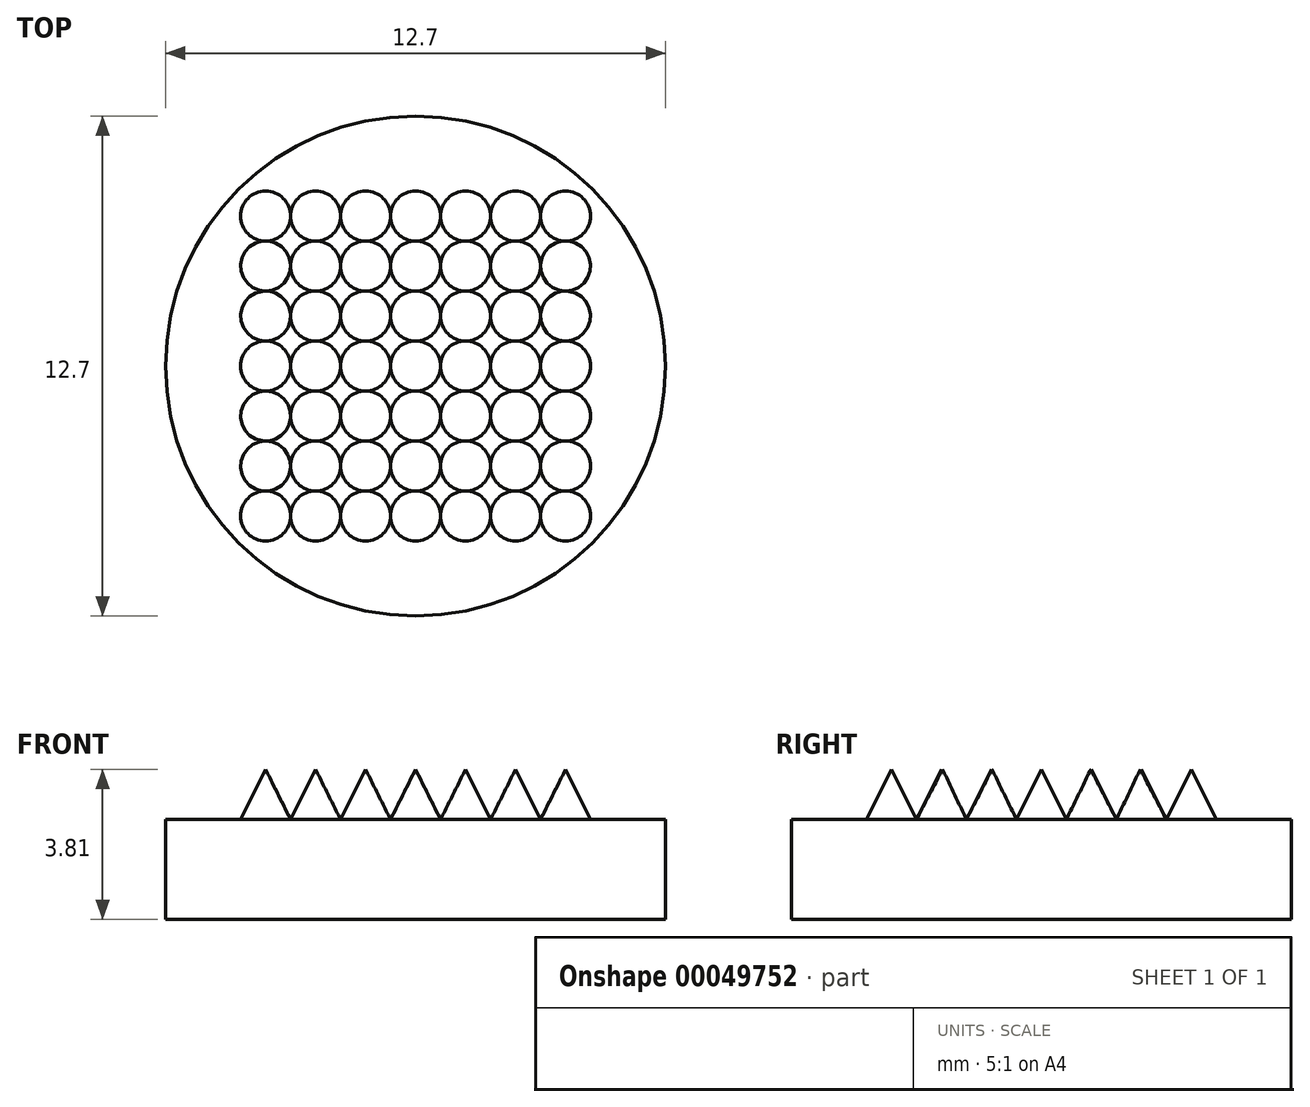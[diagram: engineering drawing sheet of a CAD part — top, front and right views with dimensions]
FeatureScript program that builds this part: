
annotation { "Feature Type Name" : "Feature", "Feature Type Description" : "" }
export const myFeature = defineFeature(function(context is Context, id is Id, definition is map)
    precondition{}
    {
        {
            var Q0;
            Q0=qCreatedBy(makeId("Top.planeOp"),FACE);
            var sketch = newSketch(context, id + "F0", { "sketchPlane" : qUnion([Q0])});
            skCircle(sketch, "E0", {"center": v(0, 0) * mm, "radius": 6.35 * mm});
            skSolve(sketch);
        }
        {
            var Q0;
            Q0=qCreatedBy(makeId("Top.planeOp"),FACE);
            var sketch = newSketch(context, id + "F1", { "sketchPlane" : qUnion([Q0])});
            skCircle(sketch, "E1", {"center": v(0, 0) * mm, "radius": 0.64 * mm});
            skCircle(sketch, "E2", {"center": v(1.27, 0) * mm, "radius": 0.64 * mm});
            skCircle(sketch, "E3", {"center": v(2.54, 0) * mm, "radius": 0.64 * mm});
            skCircle(sketch, "E4", {"center": v(1.27, -1.27) * mm, "radius": 0.64 * mm});
            skCircle(sketch, "E5", {"center": v(2.54, -1.27) * mm, "radius": 0.64 * mm});
            skCircle(sketch, "E6", {"center": v(1.27, -2.54) * mm, "radius": 0.64 * mm});
            skCircle(sketch, "E7", {"center": v(1.27, -3.81) * mm, "radius": 0.64 * mm});
            skCircle(sketch, "E8", {"center": v(2.54, -2.54) * mm, "radius": 0.64 * mm});
            skCircle(sketch, "E9", {"center": v(2.54, -3.81) * mm, "radius": 0.64 * mm});
            skCircle(sketch, "E10", {"center": v(0, -1.27) * mm, "radius": 0.64 * mm});
            skCircle(sketch, "E11", {"center": v(0, -2.54) * mm, "radius": 0.64 * mm});
            skCircle(sketch, "E12", {"center": v(0, -3.81) * mm, "radius": 0.64 * mm});
            skCircle(sketch, "E13", {"center": v(3.81, 0) * mm, "radius": 0.64 * mm});
            skCircle(sketch, "E14", {"center": v(3.81, -1.27) * mm, "radius": 0.64 * mm});
            skCircle(sketch, "E15", {"center": v(3.81, -2.54) * mm, "radius": 0.64 * mm});
            skCircle(sketch, "E16", {"center": v(3.81, -3.81) * mm, "radius": 0.64 * mm});
            skSolve(sketch);
        }
        {
            var Q0;
            Q0=makeQuery(id+"F1.imprint","IMPRINT",FACE,{"disambiguationData":[TD([[makeQuery(id+"F1.imprint","IMPRINT",EDGE,{"derivedFrom":sQuery(id+"F1.wireOp",EDGE,"E1")}),1.0]])]});
            cPlane(context, id + "F2", {"entities" : qUnion([Q0]), "cplaneType" : CPlaneType.OFFSET, "offset" : 1.27 * mm, "width" : 152.4 * mm, "height" : 152.4 * mm});
        }
        {
            var Q0;
            Q0=qCreatedBy(id+"F2.planeOp",FACE);
            var sketch = newSketch(context, id + "F3", { "sketchPlane" : qUnion([Q0])});
            skPoint(sketch, "E17", {"position": v(0, 0) * mm});
            skPoint(sketch, "E18", {"position": v(0, -1.27) * mm});
            skPoint(sketch, "E19", {"position": v(0, -2.54) * mm});
            skPoint(sketch, "E20", {"position": v(1.27, 0) * mm});
            skPoint(sketch, "E21", {"position": v(1.27, -1.27) * mm});
            skPoint(sketch, "E22", {"position": v(1.27, -2.54) * mm});
            skPoint(sketch, "E23", {"position": v(1.27, -3.81) * mm});
            skPoint(sketch, "E24", {"position": v(2.54, 0) * mm});
            skPoint(sketch, "E25", {"position": v(2.54, -1.27) * mm});
            skPoint(sketch, "E26", {"position": v(2.54, -2.54) * mm});
            skPoint(sketch, "E27", {"position": v(2.54, -3.81) * mm});
            skPoint(sketch, "E28", {"position": v(0, -3.81) * mm});
            skPoint(sketch, "E29", {"position": v(3.81, 0) * mm});
            skPoint(sketch, "E30", {"position": v(3.8, -1.25) * mm});
            skPoint(sketch, "E31", {"position": v(3.81, -2.51) * mm});
            skPoint(sketch, "E32", {"position": v(3.81, -3.81) * mm});
            skSolve(sketch);
        }
        {
            var Q0;
            {var subQ0=sQuery(id+"F1.wireOp",EDGE,"E1");var subQ1=makeQuery(id+"F1.imprint","INTERSECT",VERTEX,{"derivedFrom":[subQ0,sQuery(id+"F1.wireOp",EDGE,"E2")]});Q0=makeQuery(id+"F1.imprint","IMPRINT",FACE,{"disambiguationData":[TD([[makeQuery(id+"F1.imprint","IMPRINT",EDGE,{"disambiguationData":[TD([[subQ1,-1.0]])],"derivedFrom":subQ0}),1.0]])]});}
            var Q1;
            Q1=sQuery(id+"F3.wireOp",VERTEX,"E17");
            loft(context, id + "F4", {"sheetProfilesArray" : [{ "sheetProfileEntities" : qUnion([Q0]) }, { "sheetProfileEntities" : qUnion([Q1]) }]});
        }
        {
            var Q0;
            Q0=makeQuery(id+"F0.imprint","IMPRINT",FACE,{"disambiguationData":[TD([[makeQuery(id+"F0.imprint","IMPRINT",EDGE,{"derivedFrom":sQuery(id+"F0.wireOp",EDGE,"E0")}),1.0]])]});
            extrude(context, id + "F5", {"entities" : qUnion([Q0]), "oppositeDirection" : true, "depth" : 2.54 * mm});
        }
        {
            var Q1;
            {var subQ0=sQuery(id+"F1.wireOp",EDGE,"E10");var subQ1=makeQuery(id+"F1.imprint","INTERSECT",VERTEX,{"derivedFrom":[sQuery(id+"F1.wireOp",EDGE,"E1"),subQ0]});Q1=makeQuery(id+"F1.imprint","IMPRINT",FACE,{"disambiguationData":[TD([[makeQuery(id+"F1.imprint","IMPRINT",EDGE,{"disambiguationData":[TD([[subQ1,1.0]])],"derivedFrom":subQ0}),1.0]])]});}
            var Q2;
            Q2=sQuery(id+"F3.wireOp",VERTEX,"E18");
            loft(context, id + "F6", {"sheetProfilesArray" : [{ "sheetProfileEntities" : qUnion([Q1]) }, { "sheetProfileEntities" : qUnion([Q2]) }]});
        }
        {
            var Q1;
            {var subQ0=sQuery(id+"F1.wireOp",EDGE,"E11");var subQ1=makeQuery(id+"F1.imprint","INTERSECT",VERTEX,{"derivedFrom":[sQuery(id+"F1.wireOp",EDGE,"E10"),subQ0]});Q1=makeQuery(id+"F1.imprint","IMPRINT",FACE,{"disambiguationData":[TD([[makeQuery(id+"F1.imprint","IMPRINT",EDGE,{"disambiguationData":[TD([[subQ1,1.0]])],"derivedFrom":subQ0}),1.0]])]});}
            var Q2;
            Q2=sQuery(id+"F3.wireOp",VERTEX,"E19");
            loft(context, id + "F7", {"sheetProfilesArray" : [{ "sheetProfileEntities" : qUnion([Q1]) }, { "sheetProfileEntities" : qUnion([Q2]) }]});
        }
        {
            var Q1;
            {var subQ0=sQuery(id+"F1.wireOp",EDGE,"E12");var subQ1=makeQuery(id+"F1.imprint","INTERSECT",VERTEX,{"derivedFrom":[sQuery(id+"F1.wireOp",EDGE,"E7"),subQ0]});Q1=makeQuery(id+"F1.imprint","IMPRINT",FACE,{"disambiguationData":[TD([[makeQuery(id+"F1.imprint","IMPRINT",EDGE,{"disambiguationData":[TD([[subQ1,-1.0]])],"derivedFrom":subQ0}),1.0]])]});}
            var Q2;
            Q2=sQuery(id+"F3.wireOp",VERTEX,"E28");
            loft(context, id + "F8", {"sheetProfilesArray" : [{ "sheetProfileEntities" : qUnion([Q1]) }, { "sheetProfileEntities" : qUnion([Q2]) }]});
        }
        {
            var Q1;
            {var subQ0=sQuery(id+"F1.wireOp",EDGE,"E2");var subQ1=makeQuery(id+"F1.imprint","INTERSECT",VERTEX,{"derivedFrom":[sQuery(id+"F1.wireOp",EDGE,"E1"),subQ0]});Q1=makeQuery(id+"F1.imprint","IMPRINT",FACE,{"disambiguationData":[TD([[makeQuery(id+"F1.imprint","IMPRINT",EDGE,{"disambiguationData":[TD([[subQ1,1.0]])],"derivedFrom":subQ0}),1.0]])]});}
            var Q2;
            Q2=sQuery(id+"F3.wireOp",VERTEX,"E20");
            loft(context, id + "F9", {"sheetProfilesArray" : [{ "sheetProfileEntities" : qUnion([Q1]) }, { "sheetProfileEntities" : qUnion([Q2]) }]});
        }
        {
            var Q1;
            {var subQ0=sQuery(id+"F1.wireOp",EDGE,"E4");var subQ1=makeQuery(id+"F1.imprint","INTERSECT",VERTEX,{"derivedFrom":[sQuery(id+"F1.wireOp",EDGE,"E2"),subQ0]});Q1=makeQuery(id+"F1.imprint","IMPRINT",FACE,{"disambiguationData":[TD([[makeQuery(id+"F1.imprint","IMPRINT",EDGE,{"disambiguationData":[TD([[subQ1,1.0]])],"derivedFrom":subQ0}),1.0]])]});}
            var Q2;
            Q2=sQuery(id+"F3.wireOp",VERTEX,"E21");
            loft(context, id + "F10", {"sheetProfilesArray" : [{ "sheetProfileEntities" : qUnion([Q1]) }, { "sheetProfileEntities" : qUnion([Q2]) }]});
        }
        {
            var Q1;
            {var subQ0=sQuery(id+"F1.wireOp",EDGE,"E6");var subQ1=makeQuery(id+"F1.imprint","INTERSECT",VERTEX,{"derivedFrom":[sQuery(id+"F1.wireOp",EDGE,"E4"),subQ0]});Q1=makeQuery(id+"F1.imprint","IMPRINT",FACE,{"disambiguationData":[TD([[makeQuery(id+"F1.imprint","IMPRINT",EDGE,{"disambiguationData":[TD([[subQ1,1.0]])],"derivedFrom":subQ0}),1.0]])]});}
            var Q2;
            Q2=sQuery(id+"F3.wireOp",VERTEX,"E22");
            loft(context, id + "F11", {"sheetProfilesArray" : [{ "sheetProfileEntities" : qUnion([Q1]) }, { "sheetProfileEntities" : qUnion([Q2]) }]});
        }
        {
            var Q1;
            {var subQ0=sQuery(id+"F1.wireOp",EDGE,"E7");var subQ1=makeQuery(id+"F1.imprint","INTERSECT",VERTEX,{"derivedFrom":[subQ0,sQuery(id+"F1.wireOp",EDGE,"E9")]});Q1=makeQuery(id+"F1.imprint","IMPRINT",FACE,{"disambiguationData":[TD([[makeQuery(id+"F1.imprint","IMPRINT",EDGE,{"disambiguationData":[TD([[subQ1,-1.0]])],"derivedFrom":subQ0}),1.0]])]});}
            var Q2;
            Q2=sQuery(id+"F3.wireOp",VERTEX,"E23");
            loft(context, id + "F12", {"sheetProfilesArray" : [{ "sheetProfileEntities" : qUnion([Q1]) }, { "sheetProfileEntities" : qUnion([Q2]) }]});
        }
        {
            var Q1;
            {var subQ0=sQuery(id+"F1.wireOp",EDGE,"E3");var subQ1=makeQuery(id+"F1.imprint","INTERSECT",VERTEX,{"derivedFrom":[sQuery(id+"F1.wireOp",EDGE,"E2"),subQ0]});Q1=makeQuery(id+"F1.imprint","IMPRINT",FACE,{"disambiguationData":[TD([[makeQuery(id+"F1.imprint","IMPRINT",EDGE,{"disambiguationData":[TD([[subQ1,-1.0]])],"derivedFrom":subQ0}),1.0]])]});}
            var Q2;
            Q2=sQuery(id+"F3.wireOp",VERTEX,"E24");
            loft(context, id + "F13", {"sheetProfilesArray" : [{ "sheetProfileEntities" : qUnion([Q1]) }, { "sheetProfileEntities" : qUnion([Q2]) }]});
        }
        {
            var Q1;
            {var subQ0=sQuery(id+"F1.wireOp",EDGE,"E5");var subQ1=makeQuery(id+"F1.imprint","INTERSECT",VERTEX,{"derivedFrom":[sQuery(id+"F1.wireOp",EDGE,"E3"),subQ0]});Q1=makeQuery(id+"F1.imprint","IMPRINT",FACE,{"disambiguationData":[TD([[makeQuery(id+"F1.imprint","IMPRINT",EDGE,{"disambiguationData":[TD([[subQ1,-1.0]])],"derivedFrom":subQ0}),1.0]])]});}
            var Q2;
            Q2=sQuery(id+"F3.wireOp",VERTEX,"E25");
            loft(context, id + "F14", {"sheetProfilesArray" : [{ "sheetProfileEntities" : qUnion([Q1]) }, { "sheetProfileEntities" : qUnion([Q2]) }]});
        }
        {
            var Q1;
            {var subQ0=sQuery(id+"F1.wireOp",EDGE,"E8");var subQ1=makeQuery(id+"F1.imprint","INTERSECT",VERTEX,{"derivedFrom":[sQuery(id+"F1.wireOp",EDGE,"E5"),subQ0]});Q1=makeQuery(id+"F1.imprint","IMPRINT",FACE,{"disambiguationData":[TD([[makeQuery(id+"F1.imprint","IMPRINT",EDGE,{"disambiguationData":[TD([[subQ1,-1.0]])],"derivedFrom":subQ0}),1.0]])]});}
            var Q2;
            Q2=sQuery(id+"F3.wireOp",VERTEX,"E26");
            loft(context, id + "F15", {"sheetProfilesArray" : [{ "sheetProfileEntities" : qUnion([Q1]) }, { "sheetProfileEntities" : qUnion([Q2]) }]});
        }
        {
            var Q1;
            {var subQ0=sQuery(id+"F1.wireOp",EDGE,"E9");var subQ1=makeQuery(id+"F1.imprint","INTERSECT",VERTEX,{"derivedFrom":[sQuery(id+"F1.wireOp",EDGE,"E7"),subQ0]});Q1=makeQuery(id+"F1.imprint","IMPRINT",FACE,{"disambiguationData":[TD([[makeQuery(id+"F1.imprint","IMPRINT",EDGE,{"disambiguationData":[TD([[subQ1,1.0]])],"derivedFrom":subQ0}),1.0]])]});}
            var Q2;
            Q2=sQuery(id+"F3.wireOp",VERTEX,"E27");
            loft(context, id + "F16", {"sheetProfilesArray" : [{ "sheetProfileEntities" : qUnion([Q1]) }, { "sheetProfileEntities" : qUnion([Q2]) }]});
        }
        {
            var Q1;
            {var subQ0=sQuery(id+"F1.wireOp",EDGE,"E13");var subQ1=makeQuery(id+"F1.imprint","INTERSECT",VERTEX,{"derivedFrom":[sQuery(id+"F1.wireOp",EDGE,"E3"),subQ0]});Q1=makeQuery(id+"F1.imprint","IMPRINT",FACE,{"disambiguationData":[TD([[makeQuery(id+"F1.imprint","IMPRINT",EDGE,{"disambiguationData":[TD([[subQ1,-1.0]])],"derivedFrom":subQ0}),1.0]])]});}
            var Q2;
            Q2=sQuery(id+"F3.wireOp",VERTEX,"E29");
            loft(context, id + "F17", {"sheetProfilesArray" : [{ "sheetProfileEntities" : qUnion([Q1]) }, { "sheetProfileEntities" : qUnion([Q2]) }]});
        }
        {
            var Q1;
            {var subQ0=sQuery(id+"F1.wireOp",EDGE,"E14");var subQ1=makeQuery(id+"F1.imprint","INTERSECT",VERTEX,{"derivedFrom":[sQuery(id+"F1.wireOp",EDGE,"E13"),subQ0]});Q1=makeQuery(id+"F1.imprint","IMPRINT",FACE,{"disambiguationData":[TD([[makeQuery(id+"F1.imprint","IMPRINT",EDGE,{"disambiguationData":[TD([[subQ1,-1.0]])],"derivedFrom":subQ0}),1.0]])]});}
            var Q2;
            Q2=sQuery(id+"F3.wireOp",VERTEX,"E30");
            loft(context, id + "F18", {"sheetProfilesArray" : [{ "sheetProfileEntities" : qUnion([Q1]) }, { "sheetProfileEntities" : qUnion([Q2]) }]});
        }
        {
            var Q1;
            {var subQ0=sQuery(id+"F1.wireOp",EDGE,"E15");var subQ1=makeQuery(id+"F1.imprint","INTERSECT",VERTEX,{"derivedFrom":[sQuery(id+"F1.wireOp",EDGE,"E14"),subQ0]});Q1=makeQuery(id+"F1.imprint","IMPRINT",FACE,{"disambiguationData":[TD([[makeQuery(id+"F1.imprint","IMPRINT",EDGE,{"disambiguationData":[TD([[subQ1,-1.0]])],"derivedFrom":subQ0}),1.0]])]});}
            var Q2;
            Q2=sQuery(id+"F3.wireOp",VERTEX,"E31");
            loft(context, id + "F19", {"sheetProfilesArray" : [{ "sheetProfileEntities" : qUnion([Q1]) }, { "sheetProfileEntities" : qUnion([Q2]) }]});
        }
        {
            var Q1;
            {var subQ0=sQuery(id+"F1.wireOp",EDGE,"E16");var subQ1=makeQuery(id+"F1.imprint","INTERSECT",VERTEX,{"derivedFrom":[sQuery(id+"F1.wireOp",EDGE,"E9"),subQ0]});Q1=makeQuery(id+"F1.imprint","IMPRINT",FACE,{"disambiguationData":[TD([[makeQuery(id+"F1.imprint","IMPRINT",EDGE,{"disambiguationData":[TD([[subQ1,1.0]])],"derivedFrom":subQ0}),1.0]])]});}
            var Q2;
            Q2=sQuery(id+"F3.wireOp",VERTEX,"E32");
            loft(context, id + "F20", {"sheetProfilesArray" : [{ "sheetProfileEntities" : qUnion([Q1]) }, { "sheetProfileEntities" : qUnion([Q2]) }]});
        }
        {
            var Q0;
            {var subQ0=sQuery(id+"F1.wireOp",EDGE,"E1");var subQ1=makeQuery(id+"F1.imprint","INTERSECT",VERTEX,{"derivedFrom":[subQ0,sQuery(id+"F1.wireOp",EDGE,"E2")]});Q0=makeQuery(id+"F4.opLoft","SWEPT_BODY",BODY,{"disambiguationData":[OSD([makeQuery(id+"F1.imprint","IMPRINT",FACE,{"disambiguationData":[TD([[makeQuery(id+"F1.imprint","IMPRINT",EDGE,{"disambiguationData":[TD([[subQ1,-1.0]])],"derivedFrom":subQ0}),1.0]])]}),sQuery(id+"F3.wireOp",VERTEX,"E17")])]});}
            var Q1;
            {var subQ0=sQuery(id+"F1.wireOp",EDGE,"E10");var subQ1=makeQuery(id+"F1.imprint","INTERSECT",VERTEX,{"derivedFrom":[sQuery(id+"F1.wireOp",EDGE,"E1"),subQ0]});Q1=makeQuery(id+"F6.opLoft","SWEPT_BODY",BODY,{"disambiguationData":[OSD([makeQuery(id+"F1.imprint","IMPRINT",FACE,{"disambiguationData":[TD([[makeQuery(id+"F1.imprint","IMPRINT",EDGE,{"disambiguationData":[TD([[subQ1,1.0]])],"derivedFrom":subQ0}),1.0]])]}),sQuery(id+"F3.wireOp",VERTEX,"E18")])]});}
            var Q2;
            {var subQ0=sQuery(id+"F1.wireOp",EDGE,"E11");var subQ1=makeQuery(id+"F1.imprint","INTERSECT",VERTEX,{"derivedFrom":[sQuery(id+"F1.wireOp",EDGE,"E10"),subQ0]});Q2=makeQuery(id+"F7.opLoft","SWEPT_BODY",BODY,{"disambiguationData":[OSD([makeQuery(id+"F1.imprint","IMPRINT",FACE,{"disambiguationData":[TD([[makeQuery(id+"F1.imprint","IMPRINT",EDGE,{"disambiguationData":[TD([[subQ1,1.0]])],"derivedFrom":subQ0}),1.0]])]}),sQuery(id+"F3.wireOp",VERTEX,"E19")])]});}
            var Q3;
            {var subQ0=sQuery(id+"F1.wireOp",EDGE,"E12");var subQ1=makeQuery(id+"F1.imprint","INTERSECT",VERTEX,{"derivedFrom":[sQuery(id+"F1.wireOp",EDGE,"E7"),subQ0]});Q3=makeQuery(id+"F8.opLoft","SWEPT_BODY",BODY,{"disambiguationData":[OSD([makeQuery(id+"F1.imprint","IMPRINT",FACE,{"disambiguationData":[TD([[makeQuery(id+"F1.imprint","IMPRINT",EDGE,{"disambiguationData":[TD([[subQ1,-1.0]])],"derivedFrom":subQ0}),1.0]])]}),sQuery(id+"F3.wireOp",VERTEX,"E28")])]});}
            var Q4;
            {var subQ0=sQuery(id+"F1.wireOp",EDGE,"E7");var subQ1=makeQuery(id+"F1.imprint","INTERSECT",VERTEX,{"derivedFrom":[subQ0,sQuery(id+"F1.wireOp",EDGE,"E9")]});Q4=makeQuery(id+"F12.opLoft","SWEPT_BODY",BODY,{"disambiguationData":[OSD([makeQuery(id+"F1.imprint","IMPRINT",FACE,{"disambiguationData":[TD([[makeQuery(id+"F1.imprint","IMPRINT",EDGE,{"disambiguationData":[TD([[subQ1,-1.0]])],"derivedFrom":subQ0}),1.0]])]}),sQuery(id+"F3.wireOp",VERTEX,"E23")])]});}
            var Q5;
            {var subQ0=sQuery(id+"F1.wireOp",EDGE,"E6");var subQ1=makeQuery(id+"F1.imprint","INTERSECT",VERTEX,{"derivedFrom":[sQuery(id+"F1.wireOp",EDGE,"E4"),subQ0]});Q5=makeQuery(id+"F11.opLoft","SWEPT_BODY",BODY,{"disambiguationData":[OSD([makeQuery(id+"F1.imprint","IMPRINT",FACE,{"disambiguationData":[TD([[makeQuery(id+"F1.imprint","IMPRINT",EDGE,{"disambiguationData":[TD([[subQ1,1.0]])],"derivedFrom":subQ0}),1.0]])]}),sQuery(id+"F3.wireOp",VERTEX,"E22")])]});}
            var Q6;
            {var subQ0=sQuery(id+"F1.wireOp",EDGE,"E4");var subQ1=makeQuery(id+"F1.imprint","INTERSECT",VERTEX,{"derivedFrom":[sQuery(id+"F1.wireOp",EDGE,"E2"),subQ0]});Q6=makeQuery(id+"F10.opLoft","SWEPT_BODY",BODY,{"disambiguationData":[OSD([makeQuery(id+"F1.imprint","IMPRINT",FACE,{"disambiguationData":[TD([[makeQuery(id+"F1.imprint","IMPRINT",EDGE,{"disambiguationData":[TD([[subQ1,1.0]])],"derivedFrom":subQ0}),1.0]])]}),sQuery(id+"F3.wireOp",VERTEX,"E21")])]});}
            var Q7;
            {var subQ0=sQuery(id+"F1.wireOp",EDGE,"E2");var subQ1=makeQuery(id+"F1.imprint","INTERSECT",VERTEX,{"derivedFrom":[sQuery(id+"F1.wireOp",EDGE,"E1"),subQ0]});Q7=makeQuery(id+"F9.opLoft","SWEPT_BODY",BODY,{"disambiguationData":[OSD([makeQuery(id+"F1.imprint","IMPRINT",FACE,{"disambiguationData":[TD([[makeQuery(id+"F1.imprint","IMPRINT",EDGE,{"disambiguationData":[TD([[subQ1,1.0]])],"derivedFrom":subQ0}),1.0]])]}),sQuery(id+"F3.wireOp",VERTEX,"E20")])]});}
            var Q8;
            {var subQ0=sQuery(id+"F1.wireOp",EDGE,"E13");var subQ1=makeQuery(id+"F1.imprint","INTERSECT",VERTEX,{"derivedFrom":[sQuery(id+"F1.wireOp",EDGE,"E3"),subQ0]});Q8=makeQuery(id+"F17.opLoft","SWEPT_BODY",BODY,{"disambiguationData":[OSD([makeQuery(id+"F1.imprint","IMPRINT",FACE,{"disambiguationData":[TD([[makeQuery(id+"F1.imprint","IMPRINT",EDGE,{"disambiguationData":[TD([[subQ1,-1.0]])],"derivedFrom":subQ0}),1.0]])]}),sQuery(id+"F3.wireOp",VERTEX,"E29")])]});}
            var Q9;
            {var subQ0=sQuery(id+"F1.wireOp",EDGE,"E3");var subQ1=makeQuery(id+"F1.imprint","INTERSECT",VERTEX,{"derivedFrom":[sQuery(id+"F1.wireOp",EDGE,"E2"),subQ0]});Q9=makeQuery(id+"F13.opLoft","SWEPT_BODY",BODY,{"disambiguationData":[OSD([makeQuery(id+"F1.imprint","IMPRINT",FACE,{"disambiguationData":[TD([[makeQuery(id+"F1.imprint","IMPRINT",EDGE,{"disambiguationData":[TD([[subQ1,1.0]])],"derivedFrom":subQ0}),1.0]])]}),sQuery(id+"F3.wireOp",VERTEX,"E24")])]});}
            var Q10;
            {var subQ0=sQuery(id+"F1.wireOp",EDGE,"E5");var subQ1=makeQuery(id+"F1.imprint","INTERSECT",VERTEX,{"derivedFrom":[sQuery(id+"F1.wireOp",EDGE,"E3"),subQ0]});Q10=makeQuery(id+"F14.opLoft","SWEPT_BODY",BODY,{"disambiguationData":[OSD([makeQuery(id+"F1.imprint","IMPRINT",FACE,{"disambiguationData":[TD([[makeQuery(id+"F1.imprint","IMPRINT",EDGE,{"disambiguationData":[TD([[subQ1,1.0]])],"derivedFrom":subQ0}),1.0]])]}),sQuery(id+"F3.wireOp",VERTEX,"E25")])]});}
            var Q11;
            {var subQ0=sQuery(id+"F1.wireOp",EDGE,"E14");var subQ1=makeQuery(id+"F1.imprint","INTERSECT",VERTEX,{"derivedFrom":[sQuery(id+"F1.wireOp",EDGE,"E13"),subQ0]});Q11=makeQuery(id+"F18.opLoft","SWEPT_BODY",BODY,{"disambiguationData":[OSD([makeQuery(id+"F1.imprint","IMPRINT",FACE,{"disambiguationData":[TD([[makeQuery(id+"F1.imprint","IMPRINT",EDGE,{"disambiguationData":[TD([[subQ1,-1.0]])],"derivedFrom":subQ0}),1.0]])]}),sQuery(id+"F3.wireOp",VERTEX,"E30")])]});}
            var Q12;
            {var subQ0=sQuery(id+"F1.wireOp",EDGE,"E15");var subQ1=makeQuery(id+"F1.imprint","INTERSECT",VERTEX,{"derivedFrom":[sQuery(id+"F1.wireOp",EDGE,"E14"),subQ0]});Q12=makeQuery(id+"F19.opLoft","SWEPT_BODY",BODY,{"disambiguationData":[OSD([makeQuery(id+"F1.imprint","IMPRINT",FACE,{"disambiguationData":[TD([[makeQuery(id+"F1.imprint","IMPRINT",EDGE,{"disambiguationData":[TD([[subQ1,-1.0]])],"derivedFrom":subQ0}),1.0]])]}),sQuery(id+"F3.wireOp",VERTEX,"E31")])]});}
            var Q13;
            {var subQ0=sQuery(id+"F1.wireOp",EDGE,"E8");var subQ1=makeQuery(id+"F1.imprint","INTERSECT",VERTEX,{"derivedFrom":[sQuery(id+"F1.wireOp",EDGE,"E5"),subQ0]});Q13=makeQuery(id+"F15.opLoft","SWEPT_BODY",BODY,{"disambiguationData":[OSD([makeQuery(id+"F1.imprint","IMPRINT",FACE,{"disambiguationData":[TD([[makeQuery(id+"F1.imprint","IMPRINT",EDGE,{"disambiguationData":[TD([[subQ1,1.0]])],"derivedFrom":subQ0}),1.0]])]}),sQuery(id+"F3.wireOp",VERTEX,"E26")])]});}
            var Q14;
            {var subQ0=sQuery(id+"F1.wireOp",EDGE,"E9");var subQ1=makeQuery(id+"F1.imprint","INTERSECT",VERTEX,{"derivedFrom":[subQ0,sQuery(id+"F1.wireOp",EDGE,"E16")]});Q14=makeQuery(id+"F16.opLoft","SWEPT_BODY",BODY,{"disambiguationData":[OSD([makeQuery(id+"F1.imprint","IMPRINT",FACE,{"disambiguationData":[TD([[makeQuery(id+"F1.imprint","IMPRINT",EDGE,{"disambiguationData":[TD([[subQ1,-1.0]])],"derivedFrom":subQ0}),1.0]])]}),sQuery(id+"F3.wireOp",VERTEX,"E27")])]});}
            var Q15;
            {var subQ0=sQuery(id+"F1.wireOp",EDGE,"E16");var subQ1=makeQuery(id+"F1.imprint","INTERSECT",VERTEX,{"derivedFrom":[sQuery(id+"F1.wireOp",EDGE,"E9"),subQ0]});Q15=makeQuery(id+"F20.opLoft","SWEPT_BODY",BODY,{"disambiguationData":[OSD([makeQuery(id+"F1.imprint","IMPRINT",FACE,{"disambiguationData":[TD([[makeQuery(id+"F1.imprint","IMPRINT",EDGE,{"disambiguationData":[TD([[subQ1,1.0]])],"derivedFrom":subQ0}),1.0]])]}),sQuery(id+"F3.wireOp",VERTEX,"E32")])]});}
            var Q16;
            Q16=qCreatedBy(makeId("Right.planeOp"),FACE);
            mirror(context, id + "F21", {"entities" : qUnion([Q0, Q1, Q2, Q3, Q4, Q5, Q6, Q7, Q8, Q9, Q10, Q11, Q12, Q13, Q14, Q15]), "mirrorPlane" : qUnion([Q16])});
        }
        {
            var Q0;
            {var subQ0=sQuery(id+"F1.wireOp",EDGE,"E13");var subQ1=makeQuery(id+"F1.imprint","INTERSECT",VERTEX,{"derivedFrom":[sQuery(id+"F1.wireOp",EDGE,"E3"),subQ0]});Q0=makeQuery(id+"F21.opPattern","COPY",BODY,{"derivedFrom":makeQuery(id+"F17.opLoft","SWEPT_BODY",BODY,{"disambiguationData":[OSD([makeQuery(id+"F1.imprint","IMPRINT",FACE,{"disambiguationData":[TD([[makeQuery(id+"F1.imprint","IMPRINT",EDGE,{"disambiguationData":[TD([[subQ1,-1.0]])],"derivedFrom":subQ0}),1.0]])]}),sQuery(id+"F3.wireOp",VERTEX,"E29")])]}),"instanceName":"1"});}
            var Q1;
            {var subQ0=sQuery(id+"F1.wireOp",EDGE,"E14");var subQ1=makeQuery(id+"F1.imprint","INTERSECT",VERTEX,{"derivedFrom":[sQuery(id+"F1.wireOp",EDGE,"E13"),subQ0]});Q1=makeQuery(id+"F21.opPattern","COPY",BODY,{"derivedFrom":makeQuery(id+"F18.opLoft","SWEPT_BODY",BODY,{"disambiguationData":[OSD([makeQuery(id+"F1.imprint","IMPRINT",FACE,{"disambiguationData":[TD([[makeQuery(id+"F1.imprint","IMPRINT",EDGE,{"disambiguationData":[TD([[subQ1,-1.0]])],"derivedFrom":subQ0}),1.0]])]}),sQuery(id+"F3.wireOp",VERTEX,"E30")])]}),"instanceName":"1"});}
            var Q2;
            {var subQ0=sQuery(id+"F1.wireOp",EDGE,"E15");var subQ1=makeQuery(id+"F1.imprint","INTERSECT",VERTEX,{"derivedFrom":[sQuery(id+"F1.wireOp",EDGE,"E14"),subQ0]});Q2=makeQuery(id+"F21.opPattern","COPY",BODY,{"derivedFrom":makeQuery(id+"F19.opLoft","SWEPT_BODY",BODY,{"disambiguationData":[OSD([makeQuery(id+"F1.imprint","IMPRINT",FACE,{"disambiguationData":[TD([[makeQuery(id+"F1.imprint","IMPRINT",EDGE,{"disambiguationData":[TD([[subQ1,-1.0]])],"derivedFrom":subQ0}),1.0]])]}),sQuery(id+"F3.wireOp",VERTEX,"E31")])]}),"instanceName":"1"});}
            var Q3;
            {var subQ0=sQuery(id+"F1.wireOp",EDGE,"E16");var subQ1=makeQuery(id+"F1.imprint","INTERSECT",VERTEX,{"derivedFrom":[sQuery(id+"F1.wireOp",EDGE,"E9"),subQ0]});Q3=makeQuery(id+"F21.opPattern","COPY",BODY,{"derivedFrom":makeQuery(id+"F20.opLoft","SWEPT_BODY",BODY,{"disambiguationData":[OSD([makeQuery(id+"F1.imprint","IMPRINT",FACE,{"disambiguationData":[TD([[makeQuery(id+"F1.imprint","IMPRINT",EDGE,{"disambiguationData":[TD([[subQ1,1.0]])],"derivedFrom":subQ0}),1.0]])]}),sQuery(id+"F3.wireOp",VERTEX,"E32")])]}),"instanceName":"1"});}
            var Q4;
            {var subQ0=sQuery(id+"F1.wireOp",EDGE,"E9");var subQ1=makeQuery(id+"F1.imprint","INTERSECT",VERTEX,{"derivedFrom":[subQ0,sQuery(id+"F1.wireOp",EDGE,"E16")]});Q4=makeQuery(id+"F21.opPattern","COPY",BODY,{"derivedFrom":makeQuery(id+"F16.opLoft","SWEPT_BODY",BODY,{"disambiguationData":[OSD([makeQuery(id+"F1.imprint","IMPRINT",FACE,{"disambiguationData":[TD([[makeQuery(id+"F1.imprint","IMPRINT",EDGE,{"disambiguationData":[TD([[subQ1,-1.0]])],"derivedFrom":subQ0}),1.0]])]}),sQuery(id+"F3.wireOp",VERTEX,"E27")])]}),"instanceName":"1"});}
            var Q5;
            {var subQ0=sQuery(id+"F1.wireOp",EDGE,"E8");var subQ1=makeQuery(id+"F1.imprint","INTERSECT",VERTEX,{"derivedFrom":[sQuery(id+"F1.wireOp",EDGE,"E5"),subQ0]});Q5=makeQuery(id+"F21.opPattern","COPY",BODY,{"derivedFrom":makeQuery(id+"F15.opLoft","SWEPT_BODY",BODY,{"disambiguationData":[OSD([makeQuery(id+"F1.imprint","IMPRINT",FACE,{"disambiguationData":[TD([[makeQuery(id+"F1.imprint","IMPRINT",EDGE,{"disambiguationData":[TD([[subQ1,1.0]])],"derivedFrom":subQ0}),1.0]])]}),sQuery(id+"F3.wireOp",VERTEX,"E26")])]}),"instanceName":"1"});}
            var Q6;
            {var subQ0=sQuery(id+"F1.wireOp",EDGE,"E5");var subQ1=makeQuery(id+"F1.imprint","INTERSECT",VERTEX,{"derivedFrom":[sQuery(id+"F1.wireOp",EDGE,"E3"),subQ0]});Q6=makeQuery(id+"F21.opPattern","COPY",BODY,{"derivedFrom":makeQuery(id+"F14.opLoft","SWEPT_BODY",BODY,{"disambiguationData":[OSD([makeQuery(id+"F1.imprint","IMPRINT",FACE,{"disambiguationData":[TD([[makeQuery(id+"F1.imprint","IMPRINT",EDGE,{"disambiguationData":[TD([[subQ1,1.0]])],"derivedFrom":subQ0}),1.0]])]}),sQuery(id+"F3.wireOp",VERTEX,"E25")])]}),"instanceName":"1"});}
            var Q7;
            {var subQ0=sQuery(id+"F1.wireOp",EDGE,"E3");var subQ1=makeQuery(id+"F1.imprint","INTERSECT",VERTEX,{"derivedFrom":[sQuery(id+"F1.wireOp",EDGE,"E2"),subQ0]});Q7=makeQuery(id+"F21.opPattern","COPY",BODY,{"derivedFrom":makeQuery(id+"F13.opLoft","SWEPT_BODY",BODY,{"disambiguationData":[OSD([makeQuery(id+"F1.imprint","IMPRINT",FACE,{"disambiguationData":[TD([[makeQuery(id+"F1.imprint","IMPRINT",EDGE,{"disambiguationData":[TD([[subQ1,1.0]])],"derivedFrom":subQ0}),1.0]])]}),sQuery(id+"F3.wireOp",VERTEX,"E24")])]}),"instanceName":"1"});}
            var Q8;
            {var subQ0=sQuery(id+"F1.wireOp",EDGE,"E2");var subQ1=makeQuery(id+"F1.imprint","INTERSECT",VERTEX,{"derivedFrom":[sQuery(id+"F1.wireOp",EDGE,"E1"),subQ0]});Q8=makeQuery(id+"F21.opPattern","COPY",BODY,{"derivedFrom":makeQuery(id+"F9.opLoft","SWEPT_BODY",BODY,{"disambiguationData":[OSD([makeQuery(id+"F1.imprint","IMPRINT",FACE,{"disambiguationData":[TD([[makeQuery(id+"F1.imprint","IMPRINT",EDGE,{"disambiguationData":[TD([[subQ1,1.0]])],"derivedFrom":subQ0}),1.0]])]}),sQuery(id+"F3.wireOp",VERTEX,"E20")])]}),"instanceName":"1"});}
            var Q9;
            {var subQ0=sQuery(id+"F1.wireOp",EDGE,"E4");var subQ1=makeQuery(id+"F1.imprint","INTERSECT",VERTEX,{"derivedFrom":[sQuery(id+"F1.wireOp",EDGE,"E2"),subQ0]});Q9=makeQuery(id+"F21.opPattern","COPY",BODY,{"derivedFrom":makeQuery(id+"F10.opLoft","SWEPT_BODY",BODY,{"disambiguationData":[OSD([makeQuery(id+"F1.imprint","IMPRINT",FACE,{"disambiguationData":[TD([[makeQuery(id+"F1.imprint","IMPRINT",EDGE,{"disambiguationData":[TD([[subQ1,1.0]])],"derivedFrom":subQ0}),1.0]])]}),sQuery(id+"F3.wireOp",VERTEX,"E21")])]}),"instanceName":"1"});}
            var Q10;
            {var subQ0=sQuery(id+"F1.wireOp",EDGE,"E6");var subQ1=makeQuery(id+"F1.imprint","INTERSECT",VERTEX,{"derivedFrom":[sQuery(id+"F1.wireOp",EDGE,"E4"),subQ0]});Q10=makeQuery(id+"F21.opPattern","COPY",BODY,{"derivedFrom":makeQuery(id+"F11.opLoft","SWEPT_BODY",BODY,{"disambiguationData":[OSD([makeQuery(id+"F1.imprint","IMPRINT",FACE,{"disambiguationData":[TD([[makeQuery(id+"F1.imprint","IMPRINT",EDGE,{"disambiguationData":[TD([[subQ1,1.0]])],"derivedFrom":subQ0}),1.0]])]}),sQuery(id+"F3.wireOp",VERTEX,"E22")])]}),"instanceName":"1"});}
            var Q11;
            {var subQ0=sQuery(id+"F1.wireOp",EDGE,"E7");var subQ1=makeQuery(id+"F1.imprint","INTERSECT",VERTEX,{"derivedFrom":[subQ0,sQuery(id+"F1.wireOp",EDGE,"E9")]});Q11=makeQuery(id+"F21.opPattern","COPY",BODY,{"derivedFrom":makeQuery(id+"F12.opLoft","SWEPT_BODY",BODY,{"disambiguationData":[OSD([makeQuery(id+"F1.imprint","IMPRINT",FACE,{"disambiguationData":[TD([[makeQuery(id+"F1.imprint","IMPRINT",EDGE,{"disambiguationData":[TD([[subQ1,-1.0]])],"derivedFrom":subQ0}),1.0]])]}),sQuery(id+"F3.wireOp",VERTEX,"E23")])]}),"instanceName":"1"});}
            var Q12;
            {var subQ0=sQuery(id+"F1.wireOp",EDGE,"E12");var subQ1=makeQuery(id+"F1.imprint","INTERSECT",VERTEX,{"derivedFrom":[sQuery(id+"F1.wireOp",EDGE,"E7"),subQ0]});Q12=makeQuery(id+"F8.opLoft","SWEPT_BODY",BODY,{"disambiguationData":[OSD([makeQuery(id+"F1.imprint","IMPRINT",FACE,{"disambiguationData":[TD([[makeQuery(id+"F1.imprint","IMPRINT",EDGE,{"disambiguationData":[TD([[subQ1,-1.0]])],"derivedFrom":subQ0}),1.0]])]}),sQuery(id+"F3.wireOp",VERTEX,"E28")])]});}
            var Q13;
            {var subQ0=sQuery(id+"F1.wireOp",EDGE,"E11");var subQ1=makeQuery(id+"F1.imprint","INTERSECT",VERTEX,{"derivedFrom":[sQuery(id+"F1.wireOp",EDGE,"E10"),subQ0]});Q13=makeQuery(id+"F7.opLoft","SWEPT_BODY",BODY,{"disambiguationData":[OSD([makeQuery(id+"F1.imprint","IMPRINT",FACE,{"disambiguationData":[TD([[makeQuery(id+"F1.imprint","IMPRINT",EDGE,{"disambiguationData":[TD([[subQ1,1.0]])],"derivedFrom":subQ0}),1.0]])]}),sQuery(id+"F3.wireOp",VERTEX,"E19")])]});}
            var Q14;
            {var subQ0=sQuery(id+"F1.wireOp",EDGE,"E10");var subQ1=makeQuery(id+"F1.imprint","INTERSECT",VERTEX,{"derivedFrom":[sQuery(id+"F1.wireOp",EDGE,"E1"),subQ0]});Q14=makeQuery(id+"F6.opLoft","SWEPT_BODY",BODY,{"disambiguationData":[OSD([makeQuery(id+"F1.imprint","IMPRINT",FACE,{"disambiguationData":[TD([[makeQuery(id+"F1.imprint","IMPRINT",EDGE,{"disambiguationData":[TD([[subQ1,1.0]])],"derivedFrom":subQ0}),1.0]])]}),sQuery(id+"F3.wireOp",VERTEX,"E18")])]});}
            var Q15;
            {var subQ0=sQuery(id+"F1.wireOp",EDGE,"E1");var subQ1=makeQuery(id+"F1.imprint","INTERSECT",VERTEX,{"derivedFrom":[subQ0,sQuery(id+"F1.wireOp",EDGE,"E2")]});Q15=makeQuery(id+"F4.opLoft","SWEPT_BODY",BODY,{"disambiguationData":[OSD([makeQuery(id+"F1.imprint","IMPRINT",FACE,{"disambiguationData":[TD([[makeQuery(id+"F1.imprint","IMPRINT",EDGE,{"disambiguationData":[TD([[subQ1,-1.0]])],"derivedFrom":subQ0}),1.0]])]}),sQuery(id+"F3.wireOp",VERTEX,"E17")])]});}
            var Q16;
            {var subQ0=sQuery(id+"F1.wireOp",EDGE,"E2");var subQ1=makeQuery(id+"F1.imprint","INTERSECT",VERTEX,{"derivedFrom":[sQuery(id+"F1.wireOp",EDGE,"E1"),subQ0]});Q16=makeQuery(id+"F9.opLoft","SWEPT_BODY",BODY,{"disambiguationData":[OSD([makeQuery(id+"F1.imprint","IMPRINT",FACE,{"disambiguationData":[TD([[makeQuery(id+"F1.imprint","IMPRINT",EDGE,{"disambiguationData":[TD([[subQ1,1.0]])],"derivedFrom":subQ0}),1.0]])]}),sQuery(id+"F3.wireOp",VERTEX,"E20")])]});}
            var Q17;
            {var subQ0=sQuery(id+"F1.wireOp",EDGE,"E3");var subQ1=makeQuery(id+"F1.imprint","INTERSECT",VERTEX,{"derivedFrom":[sQuery(id+"F1.wireOp",EDGE,"E2"),subQ0]});Q17=makeQuery(id+"F13.opLoft","SWEPT_BODY",BODY,{"disambiguationData":[OSD([makeQuery(id+"F1.imprint","IMPRINT",FACE,{"disambiguationData":[TD([[makeQuery(id+"F1.imprint","IMPRINT",EDGE,{"disambiguationData":[TD([[subQ1,1.0]])],"derivedFrom":subQ0}),1.0]])]}),sQuery(id+"F3.wireOp",VERTEX,"E24")])]});}
            var Q18;
            {var subQ0=sQuery(id+"F1.wireOp",EDGE,"E13");var subQ1=makeQuery(id+"F1.imprint","INTERSECT",VERTEX,{"derivedFrom":[sQuery(id+"F1.wireOp",EDGE,"E3"),subQ0]});Q18=makeQuery(id+"F17.opLoft","SWEPT_BODY",BODY,{"disambiguationData":[OSD([makeQuery(id+"F1.imprint","IMPRINT",FACE,{"disambiguationData":[TD([[makeQuery(id+"F1.imprint","IMPRINT",EDGE,{"disambiguationData":[TD([[subQ1,-1.0]])],"derivedFrom":subQ0}),1.0]])]}),sQuery(id+"F3.wireOp",VERTEX,"E29")])]});}
            var Q19;
            {var subQ0=sQuery(id+"F1.wireOp",EDGE,"E14");var subQ1=makeQuery(id+"F1.imprint","INTERSECT",VERTEX,{"derivedFrom":[sQuery(id+"F1.wireOp",EDGE,"E13"),subQ0]});Q19=makeQuery(id+"F18.opLoft","SWEPT_BODY",BODY,{"disambiguationData":[OSD([makeQuery(id+"F1.imprint","IMPRINT",FACE,{"disambiguationData":[TD([[makeQuery(id+"F1.imprint","IMPRINT",EDGE,{"disambiguationData":[TD([[subQ1,-1.0]])],"derivedFrom":subQ0}),1.0]])]}),sQuery(id+"F3.wireOp",VERTEX,"E30")])]});}
            var Q20;
            {var subQ0=sQuery(id+"F1.wireOp",EDGE,"E5");var subQ1=makeQuery(id+"F1.imprint","INTERSECT",VERTEX,{"derivedFrom":[sQuery(id+"F1.wireOp",EDGE,"E3"),subQ0]});Q20=makeQuery(id+"F14.opLoft","SWEPT_BODY",BODY,{"disambiguationData":[OSD([makeQuery(id+"F1.imprint","IMPRINT",FACE,{"disambiguationData":[TD([[makeQuery(id+"F1.imprint","IMPRINT",EDGE,{"disambiguationData":[TD([[subQ1,1.0]])],"derivedFrom":subQ0}),1.0]])]}),sQuery(id+"F3.wireOp",VERTEX,"E25")])]});}
            var Q21;
            {var subQ0=sQuery(id+"F1.wireOp",EDGE,"E4");var subQ1=makeQuery(id+"F1.imprint","INTERSECT",VERTEX,{"derivedFrom":[sQuery(id+"F1.wireOp",EDGE,"E2"),subQ0]});Q21=makeQuery(id+"F10.opLoft","SWEPT_BODY",BODY,{"disambiguationData":[OSD([makeQuery(id+"F1.imprint","IMPRINT",FACE,{"disambiguationData":[TD([[makeQuery(id+"F1.imprint","IMPRINT",EDGE,{"disambiguationData":[TD([[subQ1,1.0]])],"derivedFrom":subQ0}),1.0]])]}),sQuery(id+"F3.wireOp",VERTEX,"E21")])]});}
            var Q22;
            {var subQ0=sQuery(id+"F1.wireOp",EDGE,"E6");var subQ1=makeQuery(id+"F1.imprint","INTERSECT",VERTEX,{"derivedFrom":[sQuery(id+"F1.wireOp",EDGE,"E4"),subQ0]});Q22=makeQuery(id+"F11.opLoft","SWEPT_BODY",BODY,{"disambiguationData":[OSD([makeQuery(id+"F1.imprint","IMPRINT",FACE,{"disambiguationData":[TD([[makeQuery(id+"F1.imprint","IMPRINT",EDGE,{"disambiguationData":[TD([[subQ1,1.0]])],"derivedFrom":subQ0}),1.0]])]}),sQuery(id+"F3.wireOp",VERTEX,"E22")])]});}
            var Q23;
            {var subQ0=sQuery(id+"F1.wireOp",EDGE,"E8");var subQ1=makeQuery(id+"F1.imprint","INTERSECT",VERTEX,{"derivedFrom":[sQuery(id+"F1.wireOp",EDGE,"E5"),subQ0]});Q23=makeQuery(id+"F15.opLoft","SWEPT_BODY",BODY,{"disambiguationData":[OSD([makeQuery(id+"F1.imprint","IMPRINT",FACE,{"disambiguationData":[TD([[makeQuery(id+"F1.imprint","IMPRINT",EDGE,{"disambiguationData":[TD([[subQ1,1.0]])],"derivedFrom":subQ0}),1.0]])]}),sQuery(id+"F3.wireOp",VERTEX,"E26")])]});}
            var Q24;
            {var subQ0=sQuery(id+"F1.wireOp",EDGE,"E15");var subQ1=makeQuery(id+"F1.imprint","INTERSECT",VERTEX,{"derivedFrom":[sQuery(id+"F1.wireOp",EDGE,"E14"),subQ0]});Q24=makeQuery(id+"F19.opLoft","SWEPT_BODY",BODY,{"disambiguationData":[OSD([makeQuery(id+"F1.imprint","IMPRINT",FACE,{"disambiguationData":[TD([[makeQuery(id+"F1.imprint","IMPRINT",EDGE,{"disambiguationData":[TD([[subQ1,-1.0]])],"derivedFrom":subQ0}),1.0]])]}),sQuery(id+"F3.wireOp",VERTEX,"E31")])]});}
            var Q25;
            {var subQ0=sQuery(id+"F1.wireOp",EDGE,"E16");var subQ1=makeQuery(id+"F1.imprint","INTERSECT",VERTEX,{"derivedFrom":[sQuery(id+"F1.wireOp",EDGE,"E9"),subQ0]});Q25=makeQuery(id+"F20.opLoft","SWEPT_BODY",BODY,{"disambiguationData":[OSD([makeQuery(id+"F1.imprint","IMPRINT",FACE,{"disambiguationData":[TD([[makeQuery(id+"F1.imprint","IMPRINT",EDGE,{"disambiguationData":[TD([[subQ1,1.0]])],"derivedFrom":subQ0}),1.0]])]}),sQuery(id+"F3.wireOp",VERTEX,"E32")])]});}
            var Q26;
            {var subQ0=sQuery(id+"F1.wireOp",EDGE,"E9");var subQ1=makeQuery(id+"F1.imprint","INTERSECT",VERTEX,{"derivedFrom":[subQ0,sQuery(id+"F1.wireOp",EDGE,"E16")]});Q26=makeQuery(id+"F16.opLoft","SWEPT_BODY",BODY,{"disambiguationData":[OSD([makeQuery(id+"F1.imprint","IMPRINT",FACE,{"disambiguationData":[TD([[makeQuery(id+"F1.imprint","IMPRINT",EDGE,{"disambiguationData":[TD([[subQ1,-1.0]])],"derivedFrom":subQ0}),1.0]])]}),sQuery(id+"F3.wireOp",VERTEX,"E27")])]});}
            var Q27;
            {var subQ0=sQuery(id+"F1.wireOp",EDGE,"E7");var subQ1=makeQuery(id+"F1.imprint","INTERSECT",VERTEX,{"derivedFrom":[subQ0,sQuery(id+"F1.wireOp",EDGE,"E9")]});Q27=makeQuery(id+"F12.opLoft","SWEPT_BODY",BODY,{"disambiguationData":[OSD([makeQuery(id+"F1.imprint","IMPRINT",FACE,{"disambiguationData":[TD([[makeQuery(id+"F1.imprint","IMPRINT",EDGE,{"disambiguationData":[TD([[subQ1,-1.0]])],"derivedFrom":subQ0}),1.0]])]}),sQuery(id+"F3.wireOp",VERTEX,"E23")])]});}
            var Q28;
            Q28=qCreatedBy(makeId("Front.planeOp"),FACE);
            mirror(context, id + "F22", {"entities" : qUnion([Q0, Q1, Q2, Q3, Q4, Q5, Q6, Q7, Q8, Q9, Q10, Q11, Q12, Q13, Q14, Q15, Q16, Q17, Q18, Q19, Q20, Q21, Q22, Q23, Q24, Q25, Q26, Q27]), "mirrorPlane" : qUnion([Q28])});
        }
    });
